# Revit family: PRE030078-FR
name_source: partatom
category: Generic Models
revit_build: Autodesk Revit 2015 (Build: 20140606_1530(x64)
units: mm (PartAtom-declared; Revit-internal decimal feet)

## types (1)
- PRE030078-FR
    Adresse = 7, RUE RACINE - 92542 MONTROUGE CEDEX FRANCE
    Description = Régulateur thermostatique de sécurité 1/2" à entrées parallèles
    Débit = "Maximum : 43 L/Mn à 3 bars
Minimum : 4 L/Mn à 3 bars"
    Etape = 2
    Fabricant = LES ROBINETS PRESTO S.A.
    Finition = Corps en laiton
    Finition 1 = Material 1
    Fonction = Avec butée de température interne et entrées parallèles 1/2" (15x21)
    Garantie = 3 ans
    Hauteur = 6 cm
    Largeur = 4 cm
    Lien CCTP = http://www.prestodatashare.com
    Lien fiche produit = http://www.prestodatashare.com
    Lien notice d'utilisation = http://www.prestodatashare.com
    Manufacturer URL = http://www.prestodatashare.com
    Polantis code = PRE030078
    Pression = 2 à 5 bars
    Profondeur = 15 cm
    Raccordement = G1/2"
    Reference = 29006
    Référence = 29006
    Titre = REGULATEUR THERMOSTATIQUE ENTREE PARALLELE 1/2"
    URL = http://www.prestodatashare.com

## geometry (parser evidence)
native form markers: Sweep x2
no freeform markers — native parametric forms only
